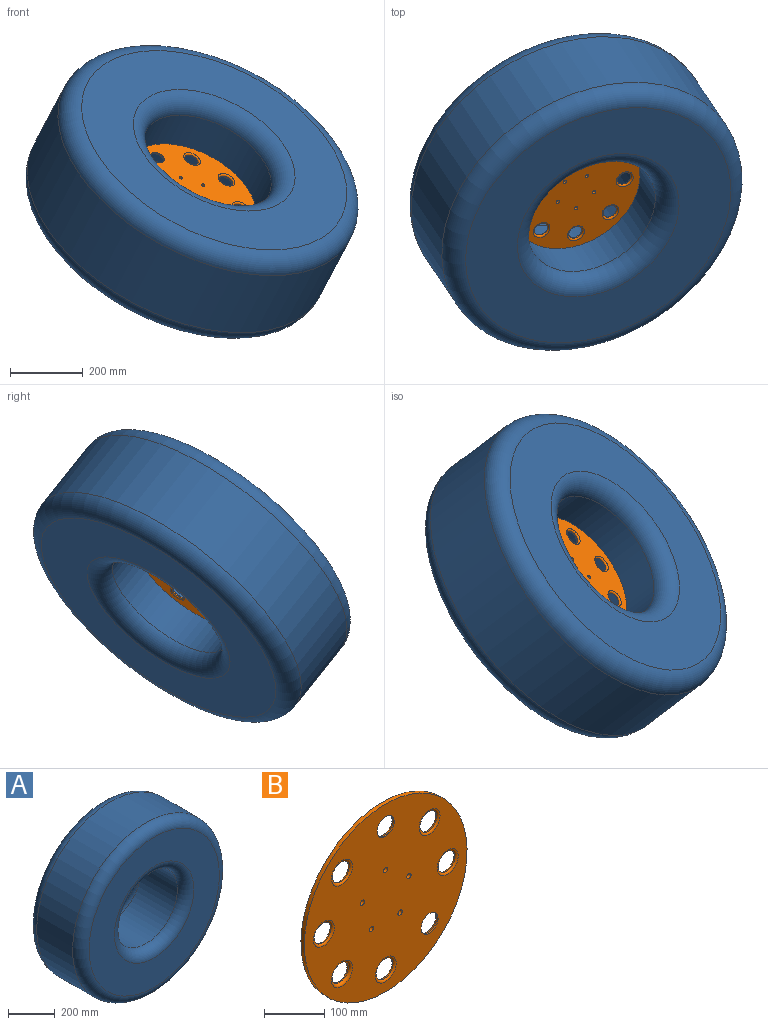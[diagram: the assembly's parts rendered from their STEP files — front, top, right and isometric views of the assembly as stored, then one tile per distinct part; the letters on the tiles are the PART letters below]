
ASSEMBLY  parts=2 mates=1
PART A: 8 faces, bbox 962.2x317.5x962.2 mm
  f0: cylinder r=190.5mm len=381mm, axis (0,1,0), area 260335.9mm2, adj f6,f7
  f1: cylinder r=444.5mm len=889mm, axis (0,1,0), area 607450.5mm2, adj f4,f5
  f2: plane 789x789mm, normal (0,-1,0), area 307216.3mm2, adj f5,f7
  f3: plane 789x789mm, normal (0,1,0), area 307216.3mm2, adj f4,f6
  f4: torus R=394.5mm, axis (0,-1,0), area 210385.9mm2, adj f1,f3
  f5: torus R=394.5mm, axis (0,-1,0), area 210385.9mm2, adj f1,f2
  f6: torus R=240.5mm, axis (0,-1,0), area 102974mm2, adj f0,f3
  f7: torus R=240.5mm, axis (0,-1,0), area 102974mm2, adj f0,f2
PART B: 24 faces, bbox 381x8.6x381 mm
  f0: cylinder r=5mm len=10mm, axis (0,1,0), area 251.3mm2, adj f5,f6
  f1: cylinder r=5mm len=10mm, axis (0,1,0), area 251.3mm2, adj f5,f6
  f2: cylinder r=5mm len=10mm, axis (0,1,0), area 251.3mm2, adj f5,f6
  f3: cylinder r=5mm len=10mm, axis (0,1,0), area 251.3mm2, adj f5,f6
  f4: cylinder r=5mm len=10mm, axis (0,1,0), area 251.3mm2, adj f5,f6
  f5: plane 381x381mm, normal (0,-1,0), area 99647.3mm2, adj f0,f1,f2,f3,f4,f7,f9,f10
  f6: plane 381x381mm, normal (0,1,0), area 98615.4mm2, adj f0,f1,f2,f3,f4,f8,f10,f11
  f7: cylinder r=20mm len=40mm, axis (0,1,0), area 377mm2, adj f5,f17
  f8: cylinder r=20mm len=40mm, axis (0,1,0), area 377mm2, adj f6,f18
  f9: cylinder r=20mm len=40mm, axis (0,1,0), area 377mm2, adj f5,f14
  f10: cylinder r=190.5mm len=381mm, axis (0,1,0), area 9575.6mm2, adj f5,f6
  f11: torus R=25mm, axis (0,-1,0), area 1076.6mm2, adj f6,f21
  f12: torus R=25mm, axis (0,-1,0), area 1076.6mm2, adj f6,f19
  f13: torus R=25mm, axis (0,-1,0), area 1076.6mm2, adj f6,f20
  f14: torus R=25mm, axis (0,-1,0), area 1076.6mm2, adj f6,f9
  f15: torus R=25mm, axis (0,-1,0), area 1076.6mm2, adj f6,f22
  f16: torus R=25mm, axis (0,-1,0), area 1076.6mm2, adj f6,f23
  f17: torus R=25mm, axis (0,-1,0), area 1076.6mm2, adj f6,f7
  f18: torus R=25mm, axis (0,-1,0), area 1076.6mm2, adj f5,f8
  f19: torus R=24.58mm, axis (0,-1,0), area 801mm2, adj f5,f12
  f20: torus R=24.58mm, axis (0,-1,0), area 801mm2, adj f5,f13
  f21: torus R=24.58mm, axis (0,-1,0), area 801mm2, adj f5,f11
  f22: torus R=24.58mm, axis (0,-1,0), area 801mm2, adj f5,f15
  f23: torus R=24.58mm, axis (0,-1,0), area 801mm2, adj f5,f16
PLACE A rot(axis=(0.98,0.2,-0.09),129.7deg) t=(310.11,-548.55,-617.56)mm
PLACE B rot(axis=(0.98,0.2,-0.09),129.7deg) t=(308.57,-546.24,-620.44)mm
MATE fastened B.f10 <-> A.f0  axis (0.38,-0.58,0.72) through (310.11,-548.55,-617.56)mm
